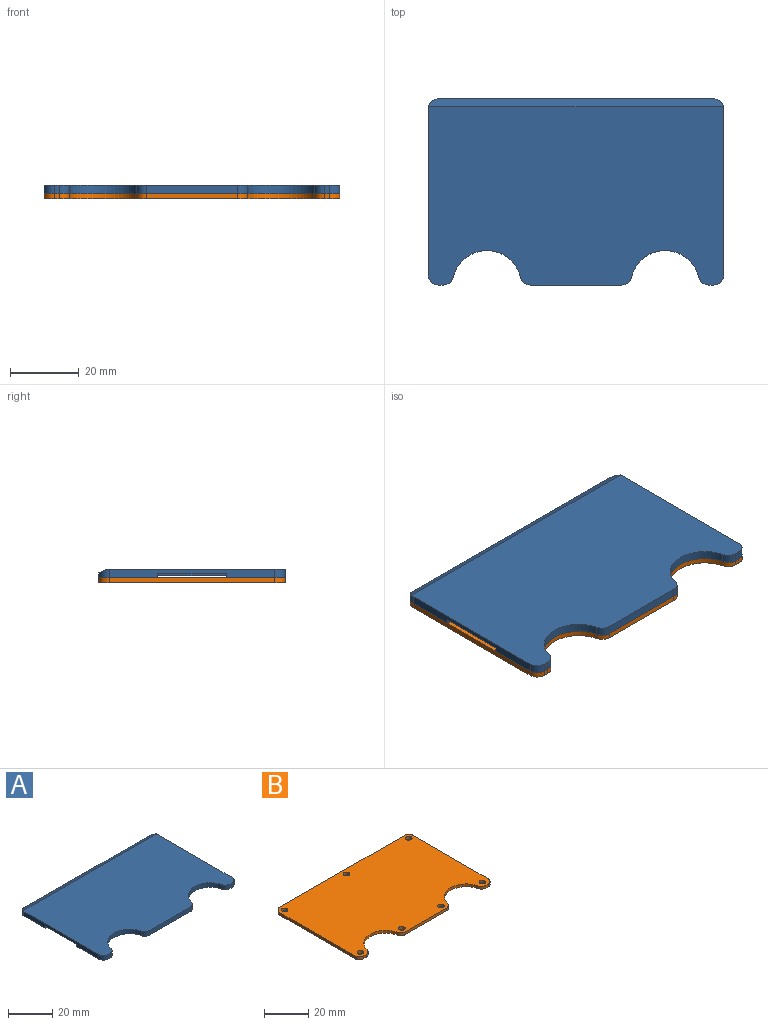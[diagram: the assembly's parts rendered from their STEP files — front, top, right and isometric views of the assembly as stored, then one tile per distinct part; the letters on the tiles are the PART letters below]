
ASSEMBLY  parts=2 mates=1
PART A: 85 faces, bbox 85.7x54x2.5 mm
  f0: plane 79.73x1.41mm, normal (0,1,0), area 112.5mm2, adj f1,f2,f23,f52
  f1: cylinder r=3mm len=3mm, axis (0,0,-1), area 9mm2, adj f0,f3,f10,f23,f52
  f2: cylinder r=3mm len=3mm, axis (0,0,-1), area 9mm2, adj f0,f3,f22,f23,f52
  f3: plane 85.73x51.68mm, normal (0,0,1), area 4106.9mm2, adj f1,f2,f10,f11,f12,f13,f14,f15
  f4: plane 20x3.46mm, normal (0,0,-1), area 69.3mm2, adj f5,f38,f47,f50
  f5: plane 85.73x1.2mm, normal (0,1,0), area 91.9mm2, adj f4,f6,f7,f8,f9,f10,f22,f39
  f6: plane 20x12.88mm, normal (0,0,-1), area 257.7mm2, adj f5,f38,f40,f46
  f7: plane 20x12.88mm, normal (0,0,-1), area 257.7mm2, adj f5,f38,f43,f49
  f8: plane 20x19.11mm, normal (0,0,-1), area 382.1mm2, adj f5,f22,f38,f41
  f9: plane 85.73x17mm, normal (0,0,-1), area 970.6mm2, adj f5,f10,f11,f12,f13,f14,f15,f16
  f10: plane 47.99x2.5mm, normal (-1,0,0), area 96mm2, adj f1,f3,f5,f9,f11,f23,f38,f39
  f11: cylinder r=3mm len=3mm, axis (0,0,-1), area 11.8mm2, adj f3,f9,f10,f12
  f12: plane 2.5x1.37mm, normal (0,-1,0), area 3.4mm2, adj f3,f9,f11,f13
  f13: cylinder r=3mm len=2.92mm, axis (0,0,-1), area 10mm2, adj f3,f9,f12,f14
  f14: cylinder r=10mm len=19.46mm, axis (0,0,-1), area 66.9mm2, adj f3,f9,f13,f15
  f15: cylinder r=3mm len=2.92mm, axis (0,0,-1), area 10mm2, adj f3,f9,f14,f16
  f16: plane 26.4x2.5mm, normal (0,-1,0), area 66mm2, adj f3,f9,f15,f17
  f17: cylinder r=3mm len=2.92mm, axis (0,0,-1), area 10mm2, adj f3,f9,f16,f18
  f18: cylinder r=10mm len=19.46mm, axis (0,0,-1), area 66.9mm2, adj f3,f9,f17,f19
  f19: cylinder r=3mm len=2.92mm, axis (0,0,-1), area 10mm2, adj f3,f9,f18,f20
  f20: plane 2.5x1.37mm, normal (0,-1,0), area 3.4mm2, adj f3,f9,f19,f21
  f21: cylinder r=3mm len=3mm, axis (0,0,-1), area 11.8mm2, adj f3,f9,f20,f22
  f22: plane 47.99x2.5mm, normal (1,0,0), area 96mm2, adj f2,f3,f5,f8,f9,f21,f23,f38
  f23: plane 85.73x17mm, normal (0,0,-1), area 920.8mm2, adj f0,f1,f2,f10,f22,f24,f26,f28
  f24: cylinder r=0.8mm len=2mm, axis (0,0,-1), area 10.1mm2, adj f23,f25
  f25: plane 1.6x1.6mm, normal (0,0,-1), area 2mm2, adj f24
  f26: cylinder r=0.8mm len=2mm, axis (0,0,-1), area 10.1mm2, adj f23,f27
  f27: plane 1.6x1.6mm, normal (0,0,-1), area 2mm2, adj f26
  f28: cylinder r=0.8mm len=2mm, axis (0,0,-1), area 10.1mm2, adj f23,f29
  f29: plane 1.6x1.6mm, normal (0,0,-1), area 2mm2, adj f28
  f30: cylinder r=0.8mm len=2mm, axis (0,0,-1), area 10.1mm2, adj f9,f31
  f31: plane 1.6x1.6mm, normal (0,0,-1), area 2mm2, adj f30
  f32: cylinder r=0.8mm len=2mm, axis (0,0,-1), area 10.1mm2, adj f9,f33
  f33: plane 1.6x1.6mm, normal (0,0,-1), area 2mm2, adj f32
  f34: cylinder r=0.8mm len=2mm, axis (0,0,-1), area 10.1mm2, adj f9,f35
  f35: plane 1.6x1.6mm, normal (0,0,-1), area 2mm2, adj f34
  f36: cylinder r=0.8mm len=2mm, axis (0,0,-1), area 10.1mm2, adj f9,f37
  f37: plane 1.6x1.6mm, normal (0,0,-1), area 2mm2, adj f36
  f38: plane 85.73x1.2mm, normal (0,-1,0), area 91.9mm2, adj f4,f6,f7,f8,f10,f22,f23,f39
  f39: plane 20x19.11mm, normal (0,0,-1), area 382.1mm2, adj f5,f10,f38,f44
  f40: plane 20x0.6mm, normal (-1,0,0), area 12mm2, adj f5,f6,f38,f42
  f41: plane 20x0.6mm, normal (1,0,0), area 12mm2, adj f5,f8,f38,f42
  f42: plane 20x4.57mm, normal (0,0,-1), area 91.4mm2, adj f5,f38,f40,f41
  f43: plane 20x0.6mm, normal (1,0,0), area 12mm2, adj f5,f7,f38,f45
  f44: plane 20x0.6mm, normal (-1,0,0), area 12mm2, adj f5,f38,f39,f45
  f45: plane 20x4.57mm, normal (0,0,-1), area 91.4mm2, adj f5,f38,f43,f44
  f46: plane 20x0.6mm, normal (1,0,0), area 12mm2, adj f5,f6,f38,f48
  f47: plane 20x0.6mm, normal (-1,0,0), area 12mm2, adj f4,f5,f38,f48
  f48: plane 20x4.57mm, normal (0,0,-1), area 91.4mm2, adj f5,f38,f46,f47
  f49: plane 20x0.6mm, normal (-1,0,0), area 12mm2, adj f5,f7,f38,f51
  f50: plane 20x0.6mm, normal (1,0,0), area 12mm2, adj f4,f5,f38,f51
  f51: plane 20x4.57mm, normal (0,0,-1), area 91.4mm2, adj f5,f38,f49,f50
  f52: plane 85.57x2.31mm, normal (0,0.43,0.9), area 215mm2, adj f0,f1,f2,f3
  f53: plane 71.73x1mm, normal (0,1,0), area 71.7mm2, adj f23,f54,f60,f61
  f54: cylinder r=2mm len=2mm, axis (0,0,-1), area 3.1mm2, adj f23,f53,f55,f61
  f55: plane 3x1mm, normal (1,0,0), area 3mm2, adj f23,f54,f56,f61
  f56: cylinder r=2mm len=2mm, axis (0,0,-1), area 3.1mm2, adj f23,f55,f57,f61
  f57: plane 71.73x1mm, normal (0,-1,0), area 71.7mm2, adj f23,f56,f58,f61
  f58: cylinder r=2mm len=2mm, axis (0,0,-1), area 3.1mm2, adj f23,f57,f59,f61
  f59: plane 3x1mm, normal (-1,0,0), area 3mm2, adj f23,f58,f60,f61
  f60: cylinder r=2mm len=2mm, axis (0,0,-1), area 3.1mm2, adj f23,f53,f59,f61
  f61: plane 75.73x7mm, normal (0,0,-1), area 526.3mm2, adj f53,f54,f55,f56,f57,f58,f59,f60
  f62: cylinder r=1mm len=1.82mm, axis (0,0,-1), area 2.5mm2, adj f9,f63,f67,f68
  f63: cylinder r=13.8mm len=3.58mm, axis (0,0,-1), area 5.1mm2, adj f9,f62,f64,f68
  f64: cylinder r=1mm len=1.83mm, axis (0,0,-1), area 2.5mm2, adj f9,f63,f65,f68
  f65: plane 3.84x1mm, normal (1,0,0), area 3.8mm2, adj f9,f64,f66,f68
  f66: cylinder r=1mm len=1mm, axis (0,0,-1), area 1.6mm2, adj f9,f65,f67,f68
  f67: plane 3.83x1mm, normal (0,-1,0), area 3.8mm2, adj f9,f62,f66,f68
  f68: plane 5.84x5.83mm, normal (0,0,-1), area 22.7mm2, adj f62,f63,f64,f65,f66,f67
  f69: cylinder r=1mm len=1.83mm, axis (0,0,-1), area 2.5mm2, adj f9,f70,f74,f75
  f70: cylinder r=13.8mm len=3.58mm, axis (0,0,-1), area 5.1mm2, adj f9,f69,f71,f75
  f71: cylinder r=1mm len=1.82mm, axis (0,0,-1), area 2.5mm2, adj f9,f70,f72,f75
  f72: plane 3.83x1mm, normal (0,-1,0), area 3.8mm2, adj f9,f71,f73,f75
  f73: cylinder r=1mm len=1mm, axis (0,0,-1), area 1.6mm2, adj f9,f72,f74,f75
  f74: plane 3.84x1mm, normal (-1,0,0), area 3.8mm2, adj f9,f69,f73,f75
  f75: plane 5.84x5.83mm, normal (0,0,-1), area 22.7mm2, adj f69,f70,f71,f72,f73,f74
  f76: cylinder r=16.2mm len=2.44mm, axis (0,0,-1), area 2.8mm2, adj f9,f77,f83,f84
  f77: cylinder r=1mm len=1mm, axis (0,0,-1), area 1.1mm2, adj f9,f76,f78,f84
  f78: plane 20.46x1mm, normal (0,1,0), area 20.5mm2, adj f9,f77,f79,f84
  f79: cylinder r=1mm len=1mm, axis (0,0,-1), area 1.1mm2, adj f9,f78,f80,f84
  f80: cylinder r=16.2mm len=2.44mm, axis (0,0,-1), area 2.8mm2, adj f9,f79,f81,f84
  f81: cylinder r=1mm len=1.57mm, axis (0,0,-1), area 2.2mm2, adj f9,f80,f82,f84
  f82: plane 23.42x1mm, normal (0,-1,0), area 23.4mm2, adj f9,f81,f83,f84
  f83: cylinder r=1mm len=1.57mm, axis (0,0,-1), area 2.2mm2, adj f9,f76,f82,f84
  f84: plane 25.42x4.6mm, normal (0,0,-1), area 109.7mm2, adj f76,f77,f78,f79,f80,f81,f82,f83
PART B: 25 faces, bbox 85.7x54x1.5 mm
  f0: plane 79.73x1.5mm, normal (0,1,0), area 119.6mm2, adj f1,f22,f23,f24
  f1: cylinder r=3mm len=3mm, axis (0,0,-1), area 7.1mm2, adj f0,f2,f23,f24
  f2: plane 47.99x1.5mm, normal (-1,0,0), area 72mm2, adj f1,f3,f23,f24
  f3: cylinder r=3mm len=3mm, axis (0,0,-1), area 7.1mm2, adj f2,f4,f23,f24
  f4: plane 1.5x1.37mm, normal (0,-1,0), area 2.1mm2, adj f3,f5,f23,f24
  f5: cylinder r=3mm len=2.92mm, axis (0,0,-1), area 6mm2, adj f4,f6,f23,f24
  f6: cylinder r=10mm len=19.46mm, axis (0,0,-1), area 40.1mm2, adj f5,f7,f23,f24
  f7: cylinder r=3mm len=2.92mm, axis (0,0,-1), area 6mm2, adj f6,f8,f23,f24
  f8: plane 26.4x1.5mm, normal (0,-1,0), area 39.6mm2, adj f7,f9,f23,f24
  f9: cylinder r=3mm len=2.92mm, axis (0,0,-1), area 6mm2, adj f8,f10,f23,f24
  f10: cylinder r=10mm len=19.46mm, axis (0,0,-1), area 40.1mm2, adj f9,f11,f23,f24
  f11: cylinder r=3mm len=2.92mm, axis (0,0,-1), area 6mm2, adj f10,f12,f23,f24
  f12: plane 1.5x1.37mm, normal (0,-1,0), area 2.1mm2, adj f11,f13,f23,f24
  f13: cylinder r=3mm len=3mm, axis (0,0,-1), area 7.1mm2, adj f12,f14,f23,f24
  f14: plane 47.99x1.5mm, normal (1,0,0), area 72mm2, adj f13,f22,f23,f24
  f15: cylinder r=1.5mm len=3mm, axis (0,0,-1), area 14.1mm2, adj f23,f24
  f16: cylinder r=1.5mm len=3mm, axis (0,0,-1), area 14.1mm2, adj f23,f24
  f17: cylinder r=1.5mm len=3mm, axis (0,0,-1), area 14.1mm2, adj f23,f24
  f18: cylinder r=1.5mm len=3mm, axis (0,0,-1), area 14.1mm2, adj f23,f24
  f19: cylinder r=1.5mm len=3mm, axis (0,0,-1), area 14.1mm2, adj f23,f24
  f20: cylinder r=1.5mm len=3mm, axis (0,0,-1), area 14.1mm2, adj f23,f24
  f21: cylinder r=1.5mm len=3mm, axis (0,0,-1), area 14.1mm2, adj f23,f24
  f22: cylinder r=3mm len=3mm, axis (0,0,-1), area 7.1mm2, adj f0,f14,f23,f24
  f23: plane 85.73x53.99mm, normal (0,0,1), area 4252mm2, adj f0,f1,f2,f3,f4,f5,f6,f7
  f24: plane 85.73x53.99mm, normal (0,0,-1), area 4252mm2, adj f0,f1,f2,f3,f4,f5,f6,f7
PLACE A t=(-11.35,-13.71,7.59)mm
PLACE B t=(-11.35,-13.71,6.09)mm
MATE fastened B.f1 <-> A.f1  axis (0,0,1) through (-51.21,10.29,7.59)mm
